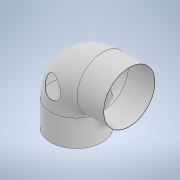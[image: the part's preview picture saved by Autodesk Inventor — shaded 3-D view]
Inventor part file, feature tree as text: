
AUTODESK INVENTOR PART (.ipt)
format: ipt  version: 2021 (Build 250183000, 183)  size: 198,144 bytes
history: native  units: mm
features: sketch x3, sweep x1, extrude x1
ambient origin geometry x8: Origin, YZ Plane, XZ Plane, XY Plane, X Axis, Y Axis, Z Axis, Center Point
bodies: Solid1 (feature_tree)
feature tree (5):
  sweep  "Sweep1"
  extrude  "Extrusion2"  Depth=20.0mm
  sketch  "Sketch1"  dims[d0=40.0mm d1=40.0mm]
  sketch  "Sketch2"  dims[d2=20.0mm d3=39.0mm]
  sketch  "Sketch4"  dims[d4=38.5mm d5=0.0mm d6=0.0mm d10=15.0mm d11=40.0mm d12=0.0mm d8=0.5mm d9=0.872665mm d13=0.5mm d14=0.872665mm]
